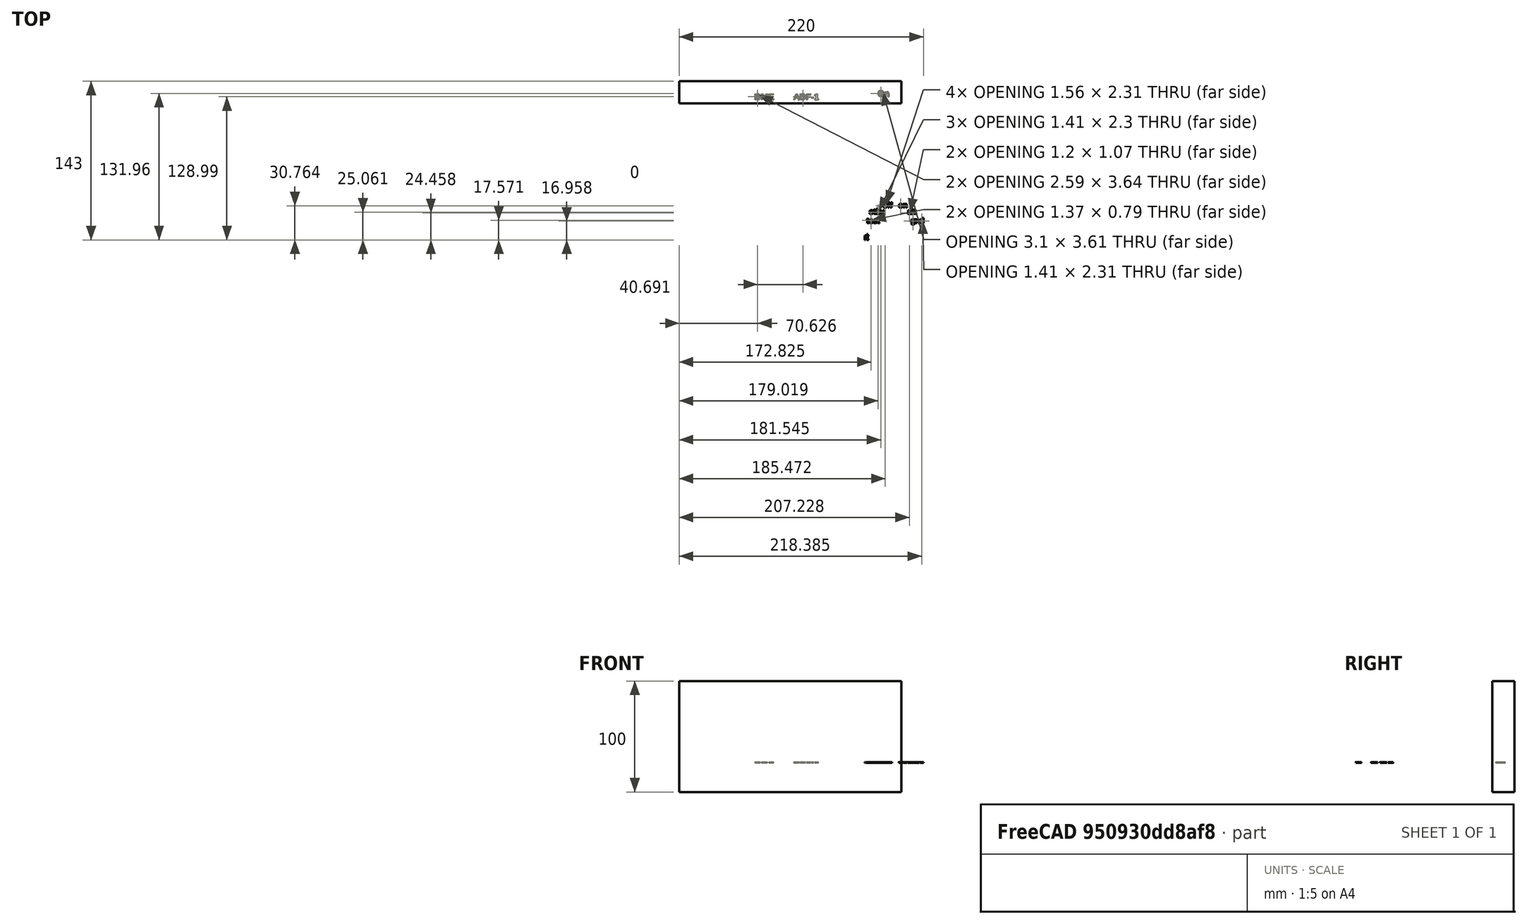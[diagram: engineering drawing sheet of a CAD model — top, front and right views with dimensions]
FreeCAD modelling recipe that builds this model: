
FCSTD DOCUMENT  (FreeCAD 0.17R13522 (Git))
Label: letritas
License: CreativeCommons Attribution-ShareAlike
LicenseURL: http://creativecommons.org/licenses/by-sa/4.0/
objects: Part::Cut×20, Part::Box×14, Part::Feature×9
note: 43 computed .brp shape members not serialized (recipe doc carries the construction recipe); baked Part::Feature solids carry a one-line shape summary decoded from their .brp

FEATURE [Part::Feature] Cut001001001002003001008002002033001001001001001001001002001001002001042002001  label="Cut001001001002003001008002002033001001001001001001001002001001002001042003"
  shape: bbox 163 x 157.9 x 19 mm, 920 faces (baked)
FEATURE [Part::Box] Box  label="apoyo_fleje_lateral"
  AttacherType = Attacher::AttachEngine3D
  Height = 2
  Length = 1.5
  Placement = pos=(129.5,-4,-105) rot=(0,0,1;0rad)
  Width = 5
FEATURE [Part::Feature] Box001  label="apoyo_fleje_lateral001"
  Placement = pos=(129.5,148.85,-105) rot=(0,0,1;0rad)
  shape: bbox 1.5 x 5 x 2 mm, 6 faces (baked)
FEATURE [Part::Feature] Box001001  label="apoyo_fleje_lateral002"
  Placement = pos=(286.5,148.85,-105) rot=(0,0,1;0rad)
  shape: bbox 1.5 x 5 x 2 mm, 6 faces (baked)
FEATURE [Part::Feature] Box001001001  label="apoyo_fleje_lateral003"
  Placement = pos=(286.5,-4,-105) rot=(0,0,1;0rad)
  shape: bbox 1.5 x 5 x 2 mm, 6 faces (baked)
FEATURE [Part::Cut] Cut
  Base = -> Cut001001001002003001008002002033001001001001001001001002001001002001042002001
  Refine = true
  Tool = -> Box001001001
FEATURE [Part::Cut] Cut001001001002003001008002002033001001001001001001001002001001002001042002002
  Base = -> Cut
  Refine = true
  Tool = -> Box001001
FEATURE [Part::Cut] Cut001001001002003001008002002033001001001001001001001002001001002001042002003
  Base = -> Cut001001001002003001008002002033001001001001001001001002001001002001042002002
  Refine = true
  Tool = -> Box
FEATURE [Part::Cut] Cut001001001002003001008002002033001001001001001001001002001001002001042002004
  Base = -> Cut001001001002003001008002002033001001001001001001001002001001002001042002003
  Refine = true
  Tool = -> Box001
FEATURE [Part::Box] Box001001002  label="Cube"
  AttacherType = Attacher::AttachEngine3D
  Height = 2
  Length = 2
  Placement = pos=(203,-4,-105) rot=(0,0,1;0rad)
  Width = 5
FEATURE [Part::Feature] Box001001002001  label="Cube001"
  Placement = pos=(203,148.85,-105) rot=(0,0,1;0rad)
  shape: bbox 2 x 5 x 2 mm, 6 faces (baked)
FEATURE [Part::Cut] Cut001001001002003001008002002033001001001001001001001002001001002001042002005
  Base = -> Cut001001001002003001008002002033001001001001001001001002001001002001042002004
  Refine = true
  Tool = -> Box001001002001
FEATURE [Part::Cut] Cut001001001002003001008002002033001001001001001001001002001001002001042002006
  Base = -> Cut001001001002003001008002002033001001001001001001001002001001002001042002005
  Refine = true
  Tool = -> Box001001002
FEATURE [Part::Box] Box001001002002  label="Cube002"
  AttacherType = Attacher::AttachEngine3D
  Height = 10
  Length = 158
  Placement = pos=(130,-4,-103.9) rot=(0,0,1;0rad)
  Width = 157.85
FEATURE [Part::Cut] Cut001001001002003001008002002033001001001001001001001002001001002001042002007
  Base = -> Box001001002002
  Refine = true
  Tool = -> Cut001001001002003001008002002033001001001001001001001002001001002001042002006
FEATURE [Part::Box] Box001001002003  label="Cube003"
  AttacherType = Attacher::AttachEngine3D
  Height = 10
  Length = 158
  Placement = pos=(130,-4,-103.1) rot=(0,0,1;0rad)
  Width = 157.85
FEATURE [Part::Cut] Cut001001001002003001008002002033001001001001001001001002001001002001042002008
  Base = -> Cut001001001002003001008002002033001001001001001001001002001001002001042002007
  Refine = true
  Tool = -> Box001001002003
FEATURE [Part::Box] Box001001002004  label="Cube004"
  AttacherType = Attacher::AttachEngine3D
  Height = 10
  Length = 214
  Placement = pos=(0,-8,-108) rot=(0,0,1;0rad)
  Width = 136
FEATURE [Part::Cut] Cut001001001002003001008002002033001001001001001001001002001001002001042002009
  Base = -> Cut001001001002003001008002002033001001001001001001001002001001002001042002008
  Refine = true
  Tool = -> Box001001002004
FEATURE [Part::Box] Box001001002005  label="Cube005"
  AttacherType = Attacher::AttachEngine3D
  Height = 10
  Length = 200
  Placement = pos=(125,146,-107) rot=(0,0,1;0rad)
  Width = 10
FEATURE [Part::Cut] Cut001001001002003001008002002033001001001001001001001002001001002001042002010
  Base = -> Cut001001001002003001008002002033001001001001001001001002001001002001042002009
  Refine = true
  Tool = -> Box001001002005
FEATURE [Part::Box] Box001001002006  label="Cube006"
  AttacherType = Attacher::AttachEngine3D
  Height = 10
  Length = 10
  Placement = pos=(151,132,-107) rot=(0,0,1;0rad)
  Width = 10
FEATURE [Part::Feature] Box001001002006001  label="Cube007"
  Placement = pos=(191,132,-107) rot=(0,0,1;0rad)
  shape: bbox 10 x 10 x 10 mm, 6 faces (baked)
FEATURE [Part::Feature] Box001001002006001001  label="Cube008"
  Placement = pos=(256,132,-107) rot=(0,0,1;0rad)
  shape: bbox 10 x 10 x 10 mm, 6 faces (baked)
FEATURE [Part::Cut] Cut001001001002003001008002002033001001001001001001001002001001002001042002011
  Base = -> Cut001001001002003001008002002033001001001001001001001002001001002001042002010
  Refine = true
  Tool = -> Box001001002006001001
FEATURE [Part::Cut] Cut001001001002003001008002002033001001001001001001001002001001002001042002012
  Base = -> Cut001001001002003001008002002033001001001001001001001002001001002001042002011
  Refine = true
  Tool = -> Box001001002006
FEATURE [Part::Cut] Cut001001001002003001008002002033001001001001001001001002001001002001042002013
  Base = -> Cut001001001002003001008002002033001001001001001001001002001001002001042002012
  Refine = true
  Tool = -> Box001001002006001
FEATURE [Part::Box] Box001001002006001002  label="Cube009"
  AttacherType = Attacher::AttachEngine3D
  Height = 10
  Length = 22
  Placement = pos=(250,50,-107) rot=(0,0,1;0rad)
  Width = 64
FEATURE [Part::Cut] Cut001001001002003001008002002033001001001001001001001002001001002001042002014
  Base = -> Cut001001001002003001008002002033001001001001001001001002001001002001042002013
  Refine = true
  Tool = -> Box001001002006001002
FEATURE [Part::Box] Box001001002006001003  label="Cube010"
  AttacherType = Attacher::AttachEngine3D
  Height = 10
  Length = 13
  Placement = pos=(219,12,-107) rot=(0,0,1;0rad)
  Width = 13
FEATURE [Part::Feature] Box001001002006001003001  label="Cube011"
  Placement = pos=(254,12,-107) rot=(0,0,1;0rad)
  shape: bbox 13 x 13 x 10 mm, 6 faces (baked)
FEATURE [Part::Cut] Cut001001001002003001008002002033001001001001001001001002001001002001042002015
  Base = -> Cut001001001002003001008002002033001001001001001001001002001001002001042002014
  Refine = true
  Tool = -> Box001001002006001003001
FEATURE [Part::Box] Box001001002006001003002  label="Cube012"
  AttacherType = Attacher::AttachEngine3D
  Height = 10
  Length = 10
  Placement = pos=(283,-7,-107) rot=(0,0,1;0rad)
  Width = 10
FEATURE [Part::Cut] Cut001001001002003001008002002033001001001001001001001002001001002001042002016
  Base = -> Cut001001001002003001008002002033001001001001001001001002001001002001042002015
  Refine = true
  Tool = -> Box001001002006001003
FEATURE [Part::Box] Box001001002006001003003  label="Cube013"
  AttacherType = Attacher::AttachEngine3D
  Height = 100
  Length = 200
  Placement = pos=(65,128,-130) rot=(0,0,1;0rad)
  Width = 20
FEATURE [Part::Cut] Cut001001001002003001008002002033001001001001001001001002001001002001042002017  label="letras_derecha"
  Base = -> Cut001001001002003001008002002033001001001001001001001002001001002001042002016
  Refine = true
  Tool = -> Box001001002006001003002
FEATURE [Part::Box] Box001001002006001003004  label="Cube014"
  AttacherType = Attacher::AttachEngine3D
  Height = 10
  Length = 34
  Placement = pos=(198,4,-108) rot=(0,0,1;0rad)
  Width = 10
FEATURE [Part::Cut] Cut001001001002003001008002002033001001001001001001001002001001002001042002018
  Base = -> Cut001001001002003001008002002033001001001001001001001002001001002001042002017
  Refine = true
  Tool = -> Box001001002006001003004
FEATURE [Part::Feature] Cut001001001002003001008002002033001001001001001001001002001001002001042002018001  label="Cut001001001002003001008002002033001001001001001001001002001001002001042002019"
  shape: bbox 151.8 x 134.7 x 0.8 mm, 611 faces, 31 solids (baked)
FEATURE [Part::Box] Box001001002006001003005  label="Cube015"
  AttacherType = Attacher::AttachEngine3D
  Height = 10
  Length = 300
  Placement = pos=(0,63,-108) rot=(0,0,1;0rad)
  Width = 200
FEATURE [Part::Cut] Cut001001001002003001008002002033001001001001001001001002001001002001042002018002
  Base = -> Cut001001001002003001008002002033001001001001001001001002001001002001042002018001
  Refine = true
  Tool = -> Box001001002006001003005
FEATURE [Part::Box] Box001001002006001003006  label="Cube016"
  AttacherType = Attacher::AttachEngine3D
  Height = 10
  Length = 22
  Placement = pos=(266.68,15.21,-106.84) rot=(0,0,1;0rad)
  Width = 10
FEATURE [Part::Cut] Cut001001001002003001008002002033001001001001001001001002001001002001042002018003
  Base = -> Cut001001001002003001008002002033001001001001001001001002001001002001042002018002
  Refine = true
  Tool = -> Box001001002006001003006
